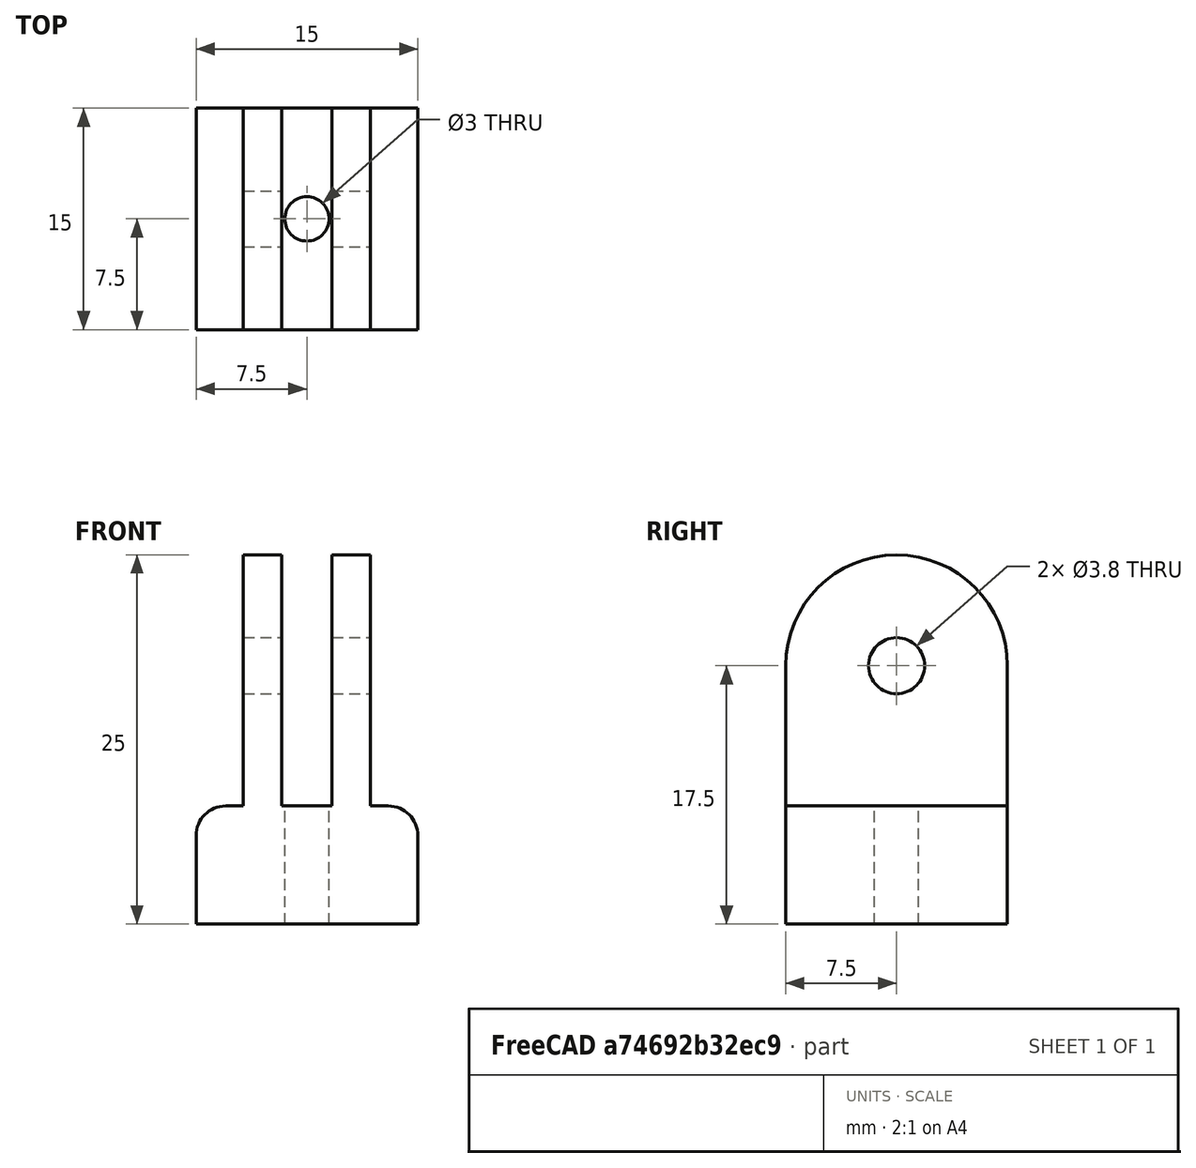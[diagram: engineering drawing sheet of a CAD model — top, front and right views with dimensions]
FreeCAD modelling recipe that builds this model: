
FCSTD DOCUMENT  (FreeCAD 0.19R23578 (Git))
Label: uv_sensor_blue
License: FreeArt
LicenseURL: http://artlibre.org/licence/lal
objects: Spreadsheet::Sheet×1, Part::Cylinder×1, Part::Box×1, Part::Feature×1, Part::Fillet×1, Part::MultiFuse×1, Part::Cut×1, App::Part×1
note: 6 computed .brp shape members not serialized (recipe doc carries the construction recipe); baked Part::Feature solids carry a one-line shape summary decoded from their .brp

FEATURE [Spreadsheet::Sheet] Spreadsheet  label="p"
  cells = A1=pcb_x; B1(pcb_x)=16; A2=pcb_y; B2(pcb_y)=21; A3=pcb_z; B3(pcb_z)=1.7; A4=hole_dist_x; B4(hole_dist_x)=15; A5=hole_off_y; B5(hole_off_y)=2.5; A6=hole_r; B6(hole_r)=1.5; A7=sensor_hole_x; B7(sensor_hole_x)=2.6; A8=wall; B8(wall)=3; A9=stick_x; B9(stick_x)=15; A10=stick_y; B10(stick_y)=15; A11=stick_length; B11(stick_length)=5
FEATURE [Part::Cylinder] Cylinder  label="bolt hole"
  Angle = 360
  AttacherType = Attacher::AttachEngine3D
  Height = 10
  Placement = pos=(7.5,7.5,0) rot=(0,0,1;0rad)
  Radius = 1.5
  expr: Radius = <<p>>.hole_r
  expr: .Placement.Base.y = <<p>>.stick_y / 2
  expr: .Placement.Base.x = <<p>>.stick_x / 2
FEATURE [Part::Box] Box002  label="stick cube"
  AttacherType = Attacher::AttachEngine3D
  Height = 5
  Length = 15
  Width = 15
  expr: Length = Spreadsheet.stick_x
  expr: Width = <<p>>.stick_y
  expr: Height = <<p>>.stick_length
FEATURE [Part::Feature] Cut001001  label="side 2 cut001"
  Placement = pos=(7.5,7.5,5) rot=(0,0,1;1.5708rad)
  shape: bbox 15 x 15 x 20 mm, 16 faces (baked)
  expr: .Placement.Base.y = <<p>>.stick_y / 2
  expr: .Placement.Base.x = Spreadsheet.stick_x / 2
  expr: .Placement.Base.z = <<p>>.stick_length
FEATURE [Part::Fillet] Fillet  label="side 2 fillet"
  Base = -> Cut001001
  Edges = 2 edges r=2: [Edge14,Edge40]
FEATURE [Part::MultiFuse] Fusion  label="holder fusion"
  Shapes = -> [Box002,Fillet]
FEATURE [Part::Cut] Cut  label="sensor cut"
  Base = -> Fusion
  Tool = -> Cylinder
FEATURE [App::Part] Part  label="UV blue sensor part"
  Group = -> [Cut]
  Origin = -> Origin
